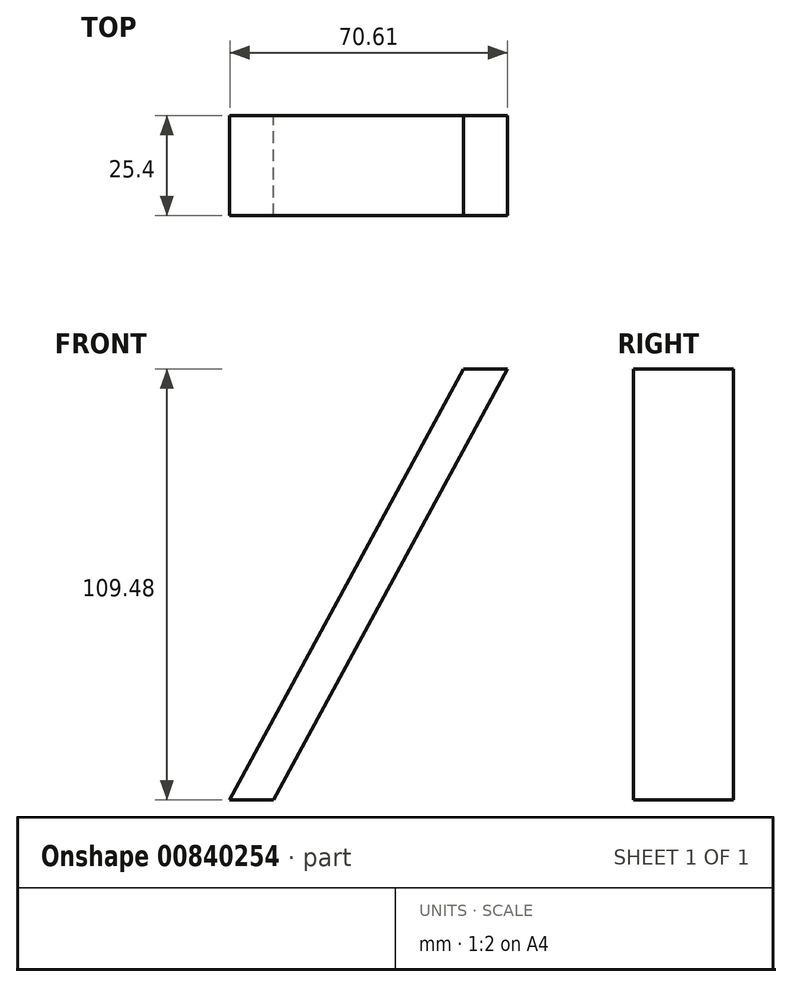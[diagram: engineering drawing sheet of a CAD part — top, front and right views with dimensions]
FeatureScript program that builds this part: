
annotation { "Feature Type Name" : "Feature", "Feature Type Description" : "" }
export const myFeature = defineFeature(function(context is Context, id is Id, definition is map)
    precondition{}
    {
        {
            var Q0;
            Q0=qCreatedBy(makeId("Front.planeOp"),FACE);
            var sketch = newSketch(context, id + "F0", { "sketchPlane" : qUnion([Q0])});
            skLineSegment(sketch, "E0", {"start": v(-51.72, -52.07) * mm, "end": v(7.71, 57.4) * mm});
            skLineSegment(sketch, "E1", {"start": v(7.71, 57.4) * mm, "end": v(18.89, 57.4) * mm});
            skLineSegment(sketch, "E2", {"start": v(18.89, 57.4) * mm, "end": v(-40.55, -52.07) * mm});
            skLineSegment(sketch, "E3", {"start": v(-51.72, -52.07) * mm, "end": v(-40.55, -52.07) * mm});
            skSolve(sketch);
        }
        {
            var Q0;
            Q0 = qSketchRegion(id + "F0", true);
            extrude(context, id + "F1", {"entities" : qUnion([Q0]), "depth" : 25.4 * mm, "offsetDistance" : 25.4 * mm});
        }
    });
